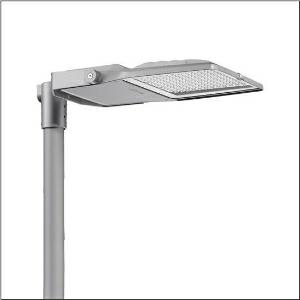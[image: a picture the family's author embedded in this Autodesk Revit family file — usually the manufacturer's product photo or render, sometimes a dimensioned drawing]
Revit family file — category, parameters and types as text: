
# Revit family: floodlight_fl_21_midi___pl64_5xa7785f2e3a_d9f8
name_source: partatom
category: Lighting Fixtures
units: mm (PartAtom-declared; Revit-internal decimal feet)

## family parameters
Cut with Voids When Loaded = No
Host = Face
Light Source = No
Part Type = Normal
Room Calculation Point = No
Round Connector Dimension = Use Diameter
Shared = No

## types (1)
- --- (1 x LED, 34530 lm, 271.6 W, 3000K)
    Apparent Load = 272 VA
    CIE Flux Codes = 28 80 98 100 100
    Color Rendering = 70
    Color Temperature = 3000K
    Default Elevation = 1800 mm
    Description = Floodlight FL 21 midi, floodlight, primary light control with lens, of PMMA, primary optical cover: protective disc, of toughened safety glass, transparent, light distribution: PL64, light emission: direct distribution, installation type: surface-mounted, LED, High Power LED, rated luminous flux: 34.530lm, luminous efficacy: 127lm/W, light colour: 730, colour temperature: 3000K, control gear: Smart Interface (Zhaga), control: flexible luminous flux parameterisation, time-dependent luminous flux control, constant luminous flux control, overheat protection, pre-setting: logarithmic dimming characteristic, with terminal, 6-pole, mains connection: 220..240V, AC, 50/60Hz, start of lifetime: 272W, end of service life: 287W, reduction: 123W, luminaire housing, of diecast aluminium, powder-coated, Siteco® metallic grey (DB 702S), corrosivity category C5 mid according to DIN EN ISO 12944, suitable for swimming pools, chlorine-resistant, sealing non-destructively replaceable, please order mast flange separately, mast bracket, of steel, galvanised, powder-coated, Siteco® metallic grey (DB 702S), Smart Interface above, protection rating (complete): IP66, insulation class (complete): insulation class II (safety insulation), certification: CE, ENEC, VDE, protection symbol: D, impact resistance: IK08, permissible operating ambient temperature: -40..+40°C, permissible operating ambient temperature for outdoor applications: -40..+50°C, standard: DIN EN 12944, LABS conformity tested according to VDMA 24364:2018-05, packaging unit: 1 piece

Light Distribution: PL64
    Height = 76 mm
    Lamp = 1 x LED
    Lamp Light Flux = 34530 lm
    Lamp Power = 271.6 W
    Lamp count = 1
    Length = 657 mm
    Luminous efficacy = 127 lm/W
    Manufacturer = Siteco
    ModVariant = No
    Model = 5XA7785F2E3A
    Number of Poles = 1
    OnlyDefault = Yes
    Power Factor = 1
    Product Name = Floodlight FL 21 midi | PL64
    Product group = floodlight | pylon annexe
    ProductGroupID = 6200
    Protection Class = Protection class II
    Protection Degree = IP 66
    RLX_Detail_Level = 1
    RLX_Emergency_Light_Flux = 0 lm
    RLX_Emergency_Type = 0
    RLX_Emergency_Type_DB = No
    RlxData = <blob elided: 153621 chars, md5=cadeda84>
    Socket = socket
    Standby Power = 0 W
    System Light Flux = 34530 lm
    System Power = 272 W
    Type Comments = factory setting: luminous flux: 100 % | dim-lin: 254 | 620 mA
    Type Image = l_1007123.jpg
    URL = http://relux.com
    VarID = @adj_180242
    Voltage = 0 V
    Weight = 0.00 kg
    Width = 442 mm

## geometry (parser evidence)
native form markers: Blend x4, Sweep x15
no freeform markers — native parametric forms only
